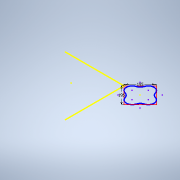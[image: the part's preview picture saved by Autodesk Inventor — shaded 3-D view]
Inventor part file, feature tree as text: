
AUTODESK INVENTOR PART (.ipt)
format: ipt  version: 2021 (Build 250183000, 183)  size: 95,744 bytes
history: native  units: in
note: dims shown in document units (in); Inventor stores cm internally (conversion verified against a paired STEP export)
features: other x3, sketch x1, reference x1
ambient origin geometry x8: Origin, YZ Plane, XZ Plane, XY Plane, X Axis, Y Axis, Z Axis, Center Point
feature tree (5):
  sketch  "Boceto1"  dims[d4=7.6772in d5=7.6772in]
  other  "Punto de trabajo1"
  reference  "Referencia1"
  other  "nsmb_peor_caso.iam"
  other  "base:1"
